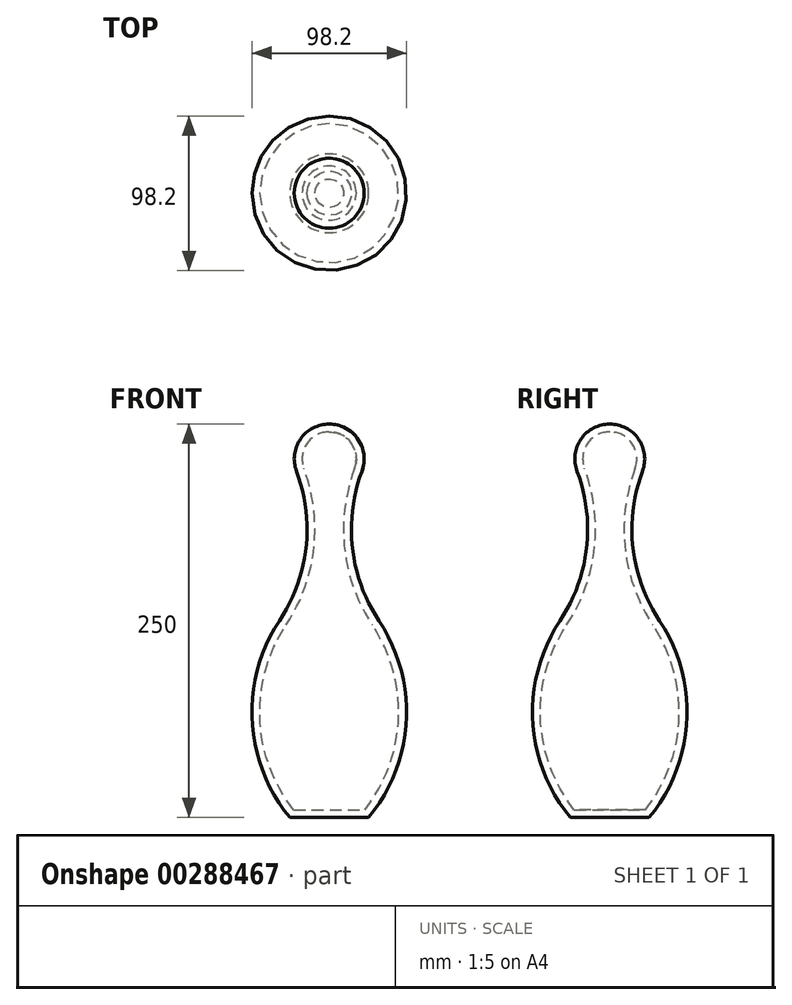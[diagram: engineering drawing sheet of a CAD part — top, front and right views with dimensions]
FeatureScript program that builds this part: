
annotation { "Feature Type Name" : "Feature", "Feature Type Description" : "" }
export const myFeature = defineFeature(function(context is Context, id is Id, definition is map)
    precondition{}
    {
        {
            var Q0;
            Q0=qCreatedBy(makeId("Front.planeOp"),FACE);
            var sketch = newSketch(context, id + "F0", { "sketchPlane" : qUnion([Q0])});
            skLineSegment(sketch, "E0", {"start": v(0, -125) * mm, "end": v(0, 125) * mm});
            skLineSegment(sketch, "E1", {"start": v(0, -125) * mm, "end": v(-25, -125) * mm});
            skArc(sketch, "E2", {"start": v(-31.58, 0) * mm, "mid": v(-48.95, -63.59) * mm, "end": v(-25, -125) * mm});
            skArc(sketch, "E3", {"start": v(-31.58, 0) * mm, "mid": v(-14.74, 46.2) * mm, "end": v(-20.78, 95) * mm});
            skArc(sketch, "E4", {"start": v(0, 125) * mm, "mid": v(-18.25, 115.44) * mm, "end": v(-20.78, 95) * mm});
            skSolve(sketch);
        }
        {
            var Q0;
            Q0=makeQuery(id+"F0.imprint","IMPRINT",FACE,{"disambiguationData":[TD([[makeQuery(id+"F0.imprint","IMPRINT",EDGE,{"derivedFrom":sQuery(id+"F0.wireOp",EDGE,"E0")}),1.0]])]});
            var Q1;
            Q1=sQuery(id+"F0.wireOp",EDGE,"E0");
            revolve(context, id + "F1", {"entities" : qUnion([Q0]), "axis" : qUnion([Q1]), "revolveType" : RevolveType.FULL});
        }
        {
            var Q0;
            Q0=makeQuery(id+"F1.opRevolve","SWEPT_FACE",FACE,{"disambiguationData":[OSD([sQuery(id+"F0.wireOp",EDGE,"E1")])]});
            var Q1;
            Q1=makeQuery(id+"F1.opRevolve","SWEPT_FACE",FACE,{"disambiguationData":[OSD([sQuery(id+"F0.wireOp",EDGE,"E2")])]});
            var Q2;
            Q2=makeQuery(id+"F1.opRevolve","SWEPT_FACE",FACE,{"disambiguationData":[OSD([sQuery(id+"F0.wireOp",EDGE,"E3")])]});
            var Q3;
            Q3=makeQuery(id+"F1.opRevolve","SWEPT_FACE",FACE,{"disambiguationData":[OSD([sQuery(id+"F0.wireOp",EDGE,"E4")])]});
            var Q4;
            Q4=makeQuery(id+"F1.opRevolve","SWEPT_BODY",BODY,{"disambiguationData":[OSD([sQuery(id+"F0.wireOp",EDGE,"E0"),sQuery(id+"F0.wireOp",EDGE,"E1"),sQuery(id+"F0.wireOp",EDGE,"E2"),sQuery(id+"F0.wireOp",EDGE,"E3"),sQuery(id+"F0.wireOp",EDGE,"E4")])]});
            shell(context, id + "F2", {"isHollow" : true, "entities" : qUnion([Q0, Q1, Q2, Q3]), "parts" : qUnion([Q4]), "thickness" : 5 * mm});
        }
    });
